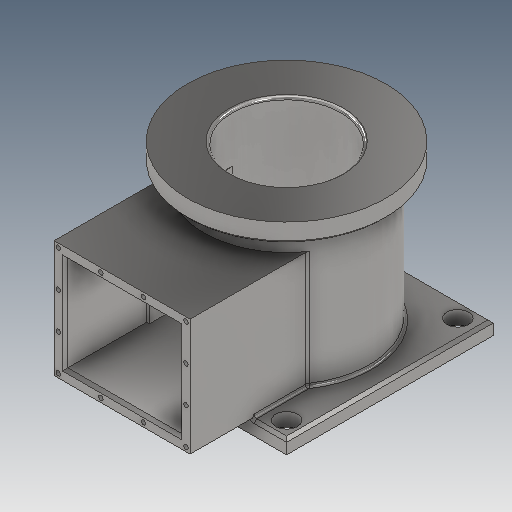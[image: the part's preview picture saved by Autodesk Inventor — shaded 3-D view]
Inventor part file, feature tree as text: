
AUTODESK INVENTOR PART (.ipt)
format: ipt  version: 2020.3 (Build 243373010, 373A)  size: 354,816 bytes
history: native  units: mm
features: extrude x9, sketch x9, fillet x5, chamfer x3, projected_geometry x3, plane x1, hole x1
ambient origin geometry x8: Origin, YZ Plane, XZ Plane, XY Plane, X Axis, Y Axis, Z Axis, Center Point
bodies: Solid1 (feature_tree)
feature tree (31):
  extrude  "Extrusion1"  Depth=35.0mm TaperAngle=0.0deg
  extrude  "Extrusion2"  TaperAngle=0.0deg  [1 undecoded]
  extrude  "Extrusion3"  Depth=305.0mm
  plane  "Work Plane1"
  sketch  "Sketch4"  dims[d8=250.0mm d9=0.0mm d10=152.5mm]
  extrude  "Extrusion4"  Depth=152.5mm
  extrude  "Extrusion5"  Depth=250.0mm
  extrude  "Extrusion6"  Depth=150.0mm TaperAngle=0.0deg
  extrude  "Extrusion7"  Depth=20.0mm
  extrude  "Extrusion8"  Depth=20.0mm
  fillet  "Fillet1"  Radius=20.0mm
  chamfer  "Chamfer1"  Distance=150.0mm
  fillet  "Fillet2"  Radius=10.0mm
  fillet  "Fillet3"  Radius=15.0mm
  chamfer  "Chamfer2"  Distance=5.0mm Angle=45.0deg
  fillet  "Fillet4"  Radius=10.0mm
  fillet  "Fillet5"  Radius=2.0mm
  chamfer  "Chamfer3"  Distance=5.0mm Angle=45.0deg
  extrude  "Extrusion9"  Depth=5.0mm
  hole  "Hole1"  [1 undecoded]
  sketch  "Sketch1"  dims[d0=365.0mm d1=35.0mm d2=0.0mm]
  sketch  "Sketch2"  dims[d3=200.0mm d4=0.0mm d5=0.0mm]
  sketch  "Sketch3"  dims[d6=365.0mm d7=305.0mm]
  projected_geometry  "Projected Loop1"
  sketch  "Sketch5"  dims[d11=215.0mm d12=250.0mm]
  sketch  "Sketch7"  dims[d13=10.0mm d14=0.0mm d15=150.0mm d16=0.0mm]
  sketch  "Sketch8"  dims[d17=25.0mm d18=0.0mm d19=20.0mm]
  projected_geometry  "Projected Loop2"
  projected_geometry  "Projected Loop3"
  sketch  "Sketch9"  dims[d20=20.0mm d21=20.0mm d22=20.0mm d23=150.0mm d24=0.0mm d25=10.0mm d26=0.0mm d27=15.0mm d28=5.0mm d29=2.0mm d30=45.0deg d31=10.0mm d32=2.0mm d33=5.0mm d34=2.0mm d35=45.0deg]
  sketch  "Sketch10"  dims[d36=5.0mm d37=5.0mm d38=5.0mm d39=2.0mm d40=45.0deg d41=40.0mm d42=30.0mm d43=30.0mm d44=40.0mm d45=30.0mm d48=40.0mm d50=30.0mm d51=40.0mm d52=30.0mm d53=30.0mm d54=10.0mm d55=0.0mm d57=380.0mm d58=380.0mm d59=250.0mm d60=15.0mm d61=15.0mm d62=7.5mm d63=7.5mm d64=40.0mm d66=78.333333mm d67=10.0mm d69=10.0mm d71=215.0mm d72=40.0mm d74=66.666667mm d75=10.0mm d77=10.0mm d79=107.5mm d80=8.376mm d81=20.0mm d82=4.0mm d83=2.0mm d84=90.0deg d85=27.3mm d86=20.594885mm]
note: 2 required parameter values undecoded (feature->parameter linkage not recoverable at this tier; creation-order binding heuristic only, values carry confidence <= 0.55)
